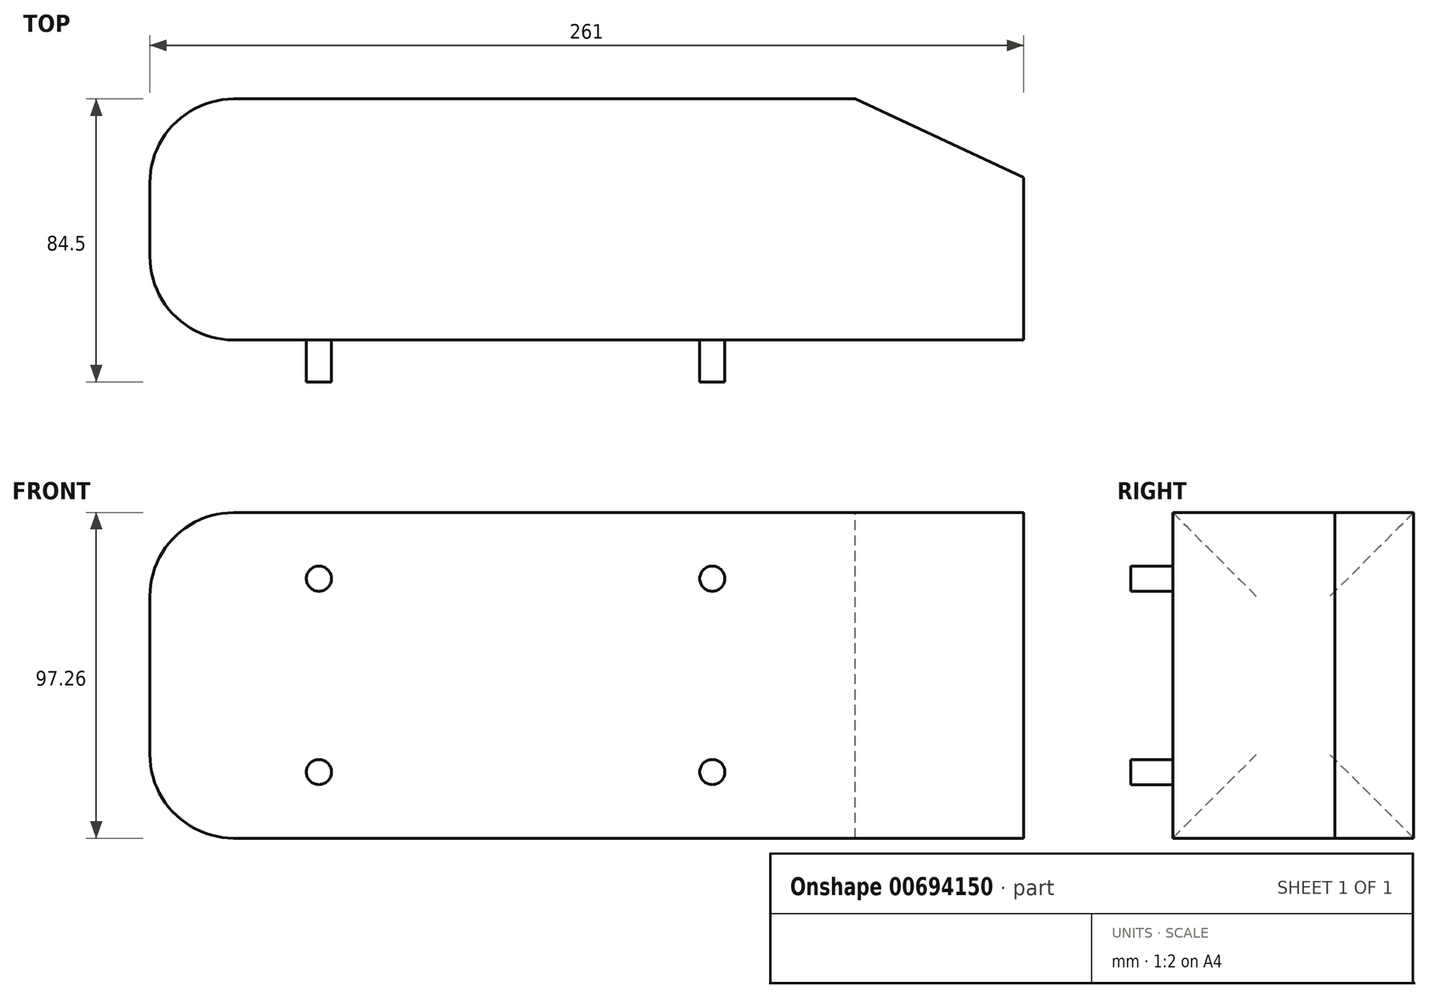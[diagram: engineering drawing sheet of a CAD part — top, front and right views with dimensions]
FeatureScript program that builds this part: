
annotation { "Feature Type Name" : "Feature", "Feature Type Description" : "" }
export const myFeature = defineFeature(function(context is Context, id is Id, definition is map)
    precondition{}
    {
        {
            var Q0;
            Q0=qCreatedBy(makeId("Front.planeOp"),FACE);
            var Q1;
            Q1 = qBodyType(qCreatedBy(id + "F1" ,EDGE), BodyType.WIRE);
            cPlane(context, id + "F0", {"entities" : qUnion([Q0, Q1]), "cplaneType" : CPlaneType.OFFSET, "offset" : 84.5 * mm, "oppositeDirection" : true, "width" : 150 * mm, "height" : 150 * mm});
        }
        {
            var Q0;
            Q0=qCreatedBy(id+"F0.planeOp",FACE);
            var sketch = newSketch(context, id + "F1", { "sketchPlane" : qUnion([Q0])});
            skPoint(sketch, "E0.middle", {"position": v(0, 0) * mm});
            skLineSegment(sketch, "E1.bottom", {"start": v(-92.85, -48.63) * mm, "end": v(92.85, -48.63) * mm});
            skLineSegment(sketch, "E1.top", {"start": v(-92.85, 48.62) * mm, "end": v(92.85, 48.62) * mm});
            skLineSegment(sketch, "E1.left", {"start": v(-92.85, -48.63) * mm, "end": v(-92.85, 48.62) * mm});
            skLineSegment(sketch, "E1.right", {"start": v(92.85, -48.63) * mm, "end": v(92.85, 48.62) * mm});
            skSolve(sketch);
        }
        {
            var Q0;
            Q0=makeQuery(id+"F1.imprint","IMPRINT",FACE,{"disambiguationData":[TD([[makeQuery(id+"F1.imprint","IMPRINT",EDGE,{"derivedFrom":sQuery(id+"F1.wireOp",EDGE,"E1.bottom")}),1.0]])]});
            extrude(context, id + "F2", {"entities" : qUnion([Q0]), "depth" : 72 * mm, "offsetDistance" : 25 * mm});
        }
        {
            var Q0;
            Q0=makeQuery(id+"F2.opExtrude","SWEPT_FACE",FACE,{"disambiguationData":[OSD([sQuery(id+"F1.wireOp",EDGE,"E1.left")])]});
            cPlane(context, id + "F3", {"entities" : qUnion([Q0]), "cplaneType" : CPlaneType.OFFSET, "offset" : 25 * mm, "width" : 150 * mm, "height" : 150 * mm});
        }
        {
            var Q0;
            Q0=qCreatedBy(id+"F3.planeOp",FACE);
            var sketch = newSketch(context, id + "F4", { "sketchPlane" : qUnion([Q0])});
            skLineSegment(sketch, "E2.bottom", {"start": v(-84.5, 48.62) * mm, "end": v(-12.5, 48.62) * mm});
            skLineSegment(sketch, "E2.top", {"start": v(-84.5, -48.63) * mm, "end": v(-12.5, -48.63) * mm});
            skLineSegment(sketch, "E2.left", {"start": v(-84.5, 48.62) * mm, "end": v(-84.5, -48.63) * mm});
            skLineSegment(sketch, "E2.right", {"start": v(-12.5, 48.62) * mm, "end": v(-12.5, -48.63) * mm});
            skPoint(sketch, "E2.middle", {"position": v(-48.5, 0) * mm});
            skSolve(sketch);
        }
        {
            var Q1;
            Q1=makeQuery(id+"F2.opExtrude","SWEPT_FACE",FACE,{"disambiguationData":[OSD([sQuery(id+"F1.wireOp",EDGE,"E1.left")])]});
            var Q2;
            Q2=makeQuery(id+"F4.imprint","IMPRINT",FACE,{"disambiguationData":[TD([[makeQuery(id+"F4.imprint","IMPRINT",EDGE,{"derivedFrom":sQuery(id+"F4.wireOp",EDGE,"E2.bottom")}),-1.0]])]});
            loft(context, id + "F5", {"operationType" : NewBodyOperationType.ADD, "sheetProfilesArray" : [{ "sheetProfileEntities" : qUnion([Q1]) }, { "sheetProfileEntities" : qUnion([Q2]) }]});
        }
        {
            var Q0;
            Q0=makeQuery(id+"F5.opLoft","MID_CAP_EDGE",EDGE,{"disambiguationData":[OSD([sQuery(id+"F4.wireOp",EDGE,"E2.bottom"),sQuery(id+"F4.wireOp",EDGE,"E2.top"),sQuery(id+"F4.wireOp",EDGE,"E2.left")])],"capPos":1.0});
            var Q1;
            Q1=makeQuery(id+"F5.opLoft","MID_CAP_EDGE",EDGE,{"disambiguationData":[OSD([sQuery(id+"F4.wireOp",EDGE,"E2.bottom"),sQuery(id+"F4.wireOp",EDGE,"E2.top"),sQuery(id+"F4.wireOp",EDGE,"E2.right")])],"capPos":1.0});
            var Q2;
            Q2=makeQuery(id+"F5.opLoft","MID_CAP_EDGE",EDGE,{"disambiguationData":[OSD([sQuery(id+"F4.wireOp",EDGE,"E2.bottom"),sQuery(id+"F4.wireOp",EDGE,"E2.left"),sQuery(id+"F4.wireOp",EDGE,"E2.right")])],"capPos":1.0});
            var Q3;
            Q3=makeQuery(id+"F5.opLoft","MID_CAP_EDGE",EDGE,{"disambiguationData":[OSD([sQuery(id+"F4.wireOp",EDGE,"E2.top"),sQuery(id+"F4.wireOp",EDGE,"E2.left"),sQuery(id+"F4.wireOp",EDGE,"E2.right")])],"capPos":1.0});
            fillet(context, id + "F6", {"entities" : qUnion([Q0, Q1, Q2, Q3]), "radius" : 25 * mm, "tangentPropagation" : true, "allowEdgeOverflow" : false});
        }
        {
            var Q0;
            Q0=makeQuery(id+"F2.opExtrude","SWEPT_FACE",FACE,{"disambiguationData":[OSD([sQuery(id+"F1.wireOp",EDGE,"E1.right")])]});
            cPlane(context, id + "F7", {"entities" : qUnion([Q0]), "cplaneType" : CPlaneType.OFFSET, "offset" : 50.3 * mm, "width" : 150 * mm, "height" : 150 * mm});
        }
        {
            var Q0;
            Q0=qCreatedBy(id+"F7.planeOp",FACE);
            var sketch = newSketch(context, id + "F8", { "sketchPlane" : qUnion([Q0])});
            skLineSegment(sketch, "E3.bottom", {"start": v(61, -48.63) * mm, "end": v(12.5, -48.63) * mm});
            skLineSegment(sketch, "E3.top", {"start": v(61, 48.62) * mm, "end": v(12.5, 48.62) * mm});
            skLineSegment(sketch, "E3.left", {"start": v(61, -48.63) * mm, "end": v(61, 48.62) * mm});
            skLineSegment(sketch, "E3.right", {"start": v(12.5, -48.63) * mm, "end": v(12.5, 48.62) * mm});
            skPoint(sketch, "E3.middle", {"position": v(36.75, 0) * mm});
            skSolve(sketch);
        }
        {
            var Q1;
            Q1=makeQuery(id+"F2.opExtrude","SWEPT_FACE",FACE,{"disambiguationData":[OSD([sQuery(id+"F1.wireOp",EDGE,"E1.right")])]});
            var Q2;
            Q2=makeQuery(id+"F8.imprint","IMPRINT",FACE,{"disambiguationData":[TD([[makeQuery(id+"F8.imprint","IMPRINT",EDGE,{"derivedFrom":sQuery(id+"F8.wireOp",EDGE,"E3.bottom")}),-1.0]])]});
            loft(context, id + "F9", {"operationType" : NewBodyOperationType.ADD, "sheetProfilesArray" : [{ "sheetProfileEntities" : qUnion([Q1]) }, { "sheetProfileEntities" : qUnion([Q2]) }]});
        }
        {
            var Q0;
            {var subQ0=sQuery(id+"F1.wireOp",EDGE,"E1.right");var subQ1=sQuery(id+"F1.wireOp",EDGE,"E1.top");var subQ2=sQuery(id+"F1.wireOp",EDGE,"E1.bottom");var subQ3=sQuery(id+"F1.wireOp",EDGE,"E1.left");Q0=makeQuery(id+"F9.boolean.opBoolean","MERGE",FACE,{"derivedFrom":[makeQuery(id+"F5.boolean.opBoolean","MERGE",FACE,{"derivedFrom":[makeQuery(id+"F2.opExtrude","CAP_FACE",FACE,{"disambiguationData":[OSD([subQ2,subQ1,subQ3,subQ0])],"isStart":false}),makeQuery(id+"F5.opLoft","SWEPT_FACE",FACE,{"disambiguationData":[OSD([subQ2,subQ1,subQ3,sQuery(id+"F4.wireOp",EDGE,"E2.bottom"),sQuery(id+"F4.wireOp",EDGE,"E2.top"),sQuery(id+"F4.wireOp",EDGE,"E2.right")])]})]}),makeQuery(id+"F9.opLoft","SWEPT_FACE",FACE,{"disambiguationData":[OSD([subQ2,subQ1,subQ0,sQuery(id+"F8.wireOp",EDGE,"E3.bottom"),sQuery(id+"F8.wireOp",EDGE,"E3.top"),sQuery(id+"F8.wireOp",EDGE,"E3.right")])]})]});}
            var sketch = newSketch(context, id + "F10", { "sketchPlane" : qUnion([Q0])});
            skCircle(sketch, "E4", {"center": v(-67.35, -28.88) * mm, "radius": 3.75 * mm});
            skCircle(sketch, "E5", {"center": v(-67.35, 28.87) * mm, "radius": 3.75 * mm});
            skCircle(sketch, "E6", {"center": v(50.15, -28.88) * mm, "radius": 3.75 * mm});
            skCircle(sketch, "E7", {"center": v(50.15, 28.87) * mm, "radius": 3.75 * mm});
            skSolve(sketch);
        }
        {
            var Q0;
            Q0=makeQuery(id+"F10.imprint","IMPRINT",FACE,{"disambiguationData":[TD([[makeQuery(id+"F10.imprint","IMPRINT",EDGE,{"derivedFrom":sQuery(id+"F10.wireOp",EDGE,"E4")}),1.0]])]});
            var Q1;
            Q1=makeQuery(id+"F10.imprint","IMPRINT",FACE,{"disambiguationData":[TD([[makeQuery(id+"F10.imprint","IMPRINT",EDGE,{"derivedFrom":sQuery(id+"F10.wireOp",EDGE,"E6")}),1.0]])]});
            var Q2;
            Q2=makeQuery(id+"F10.imprint","IMPRINT",FACE,{"disambiguationData":[TD([[makeQuery(id+"F10.imprint","IMPRINT",EDGE,{"derivedFrom":sQuery(id+"F10.wireOp",EDGE,"E7")}),1.0]])]});
            var Q3;
            Q3=makeQuery(id+"F10.imprint","IMPRINT",FACE,{"disambiguationData":[TD([[makeQuery(id+"F10.imprint","IMPRINT",EDGE,{"derivedFrom":sQuery(id+"F10.wireOp",EDGE,"E5")}),1.0]])]});
            extrude(context, id + "F11", {"entities" : qUnion([Q0, Q1, Q2, Q3]), "operationType" : NewBodyOperationType.ADD, "depth" : 12.5 * mm, "offsetDistance" : 25 * mm});
        }
    });
